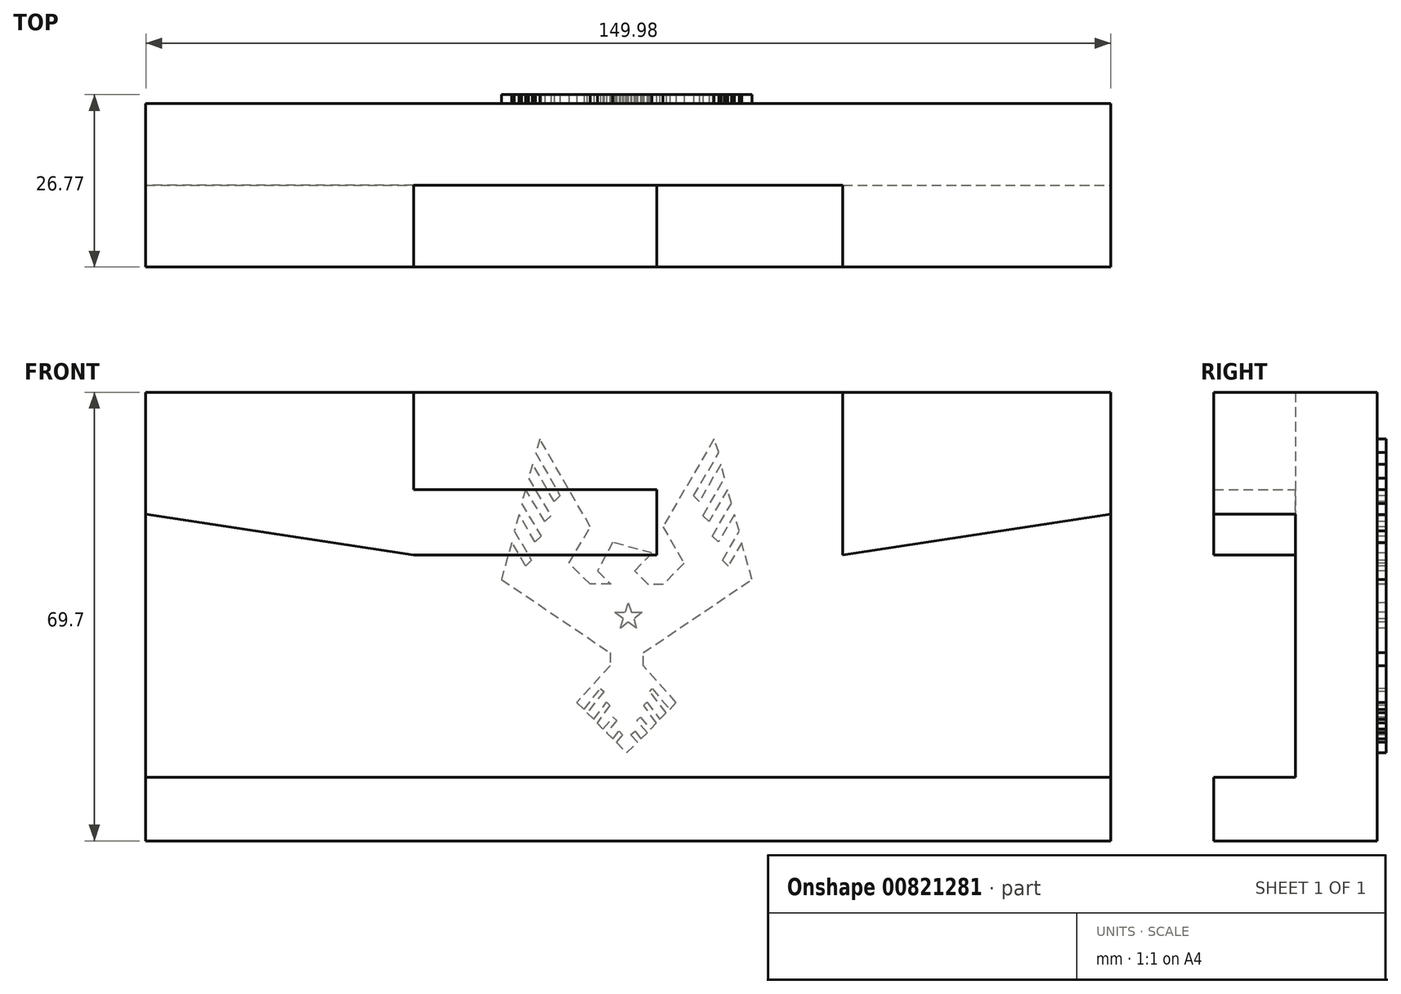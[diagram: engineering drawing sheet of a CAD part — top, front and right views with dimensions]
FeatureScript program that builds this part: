
annotation { "Feature Type Name" : "Feature", "Feature Type Description" : "" }
export const myFeature = defineFeature(function(context is Context, id is Id, definition is map)
    precondition{}
    {
        {
            var Q0;
            Q0=qCreatedBy(makeId("Front.planeOp"),FACE);
            var sketch = newSketch(context, id + "F0", { "sketchPlane" : qUnion([Q0])});
            skLineSegment(sketch, "E0.bottom", {"start": v(75, -34.85) * mm, "end": v(-75, -34.85) * mm});
            skLineSegment(sketch, "E0.top", {"start": v(75, 34.85) * mm, "end": v(-75, 34.85) * mm});
            skLineSegment(sketch, "E0.left", {"start": v(75, -34.85) * mm, "end": v(75, 34.85) * mm});
            skLineSegment(sketch, "E0.right", {"start": v(-75, -34.85) * mm, "end": v(-75, 34.85) * mm});
            skPoint(sketch, "E0.middle", {"position": v(0, 0) * mm});
            skSolve(sketch);
        }
        {
            var Q0;
            Q0=makeQuery(id+"F0.imprint","IMPRINT",FACE,{"disambiguationData":[TD([[makeQuery(id+"F0.imprint","IMPRINT",EDGE,{"derivedFrom":sQuery(id+"F0.wireOp",EDGE,"E0.bottom")}),-1.0]])]});
            extrude(context, id + "F1", {"entities" : qUnion([Q0]), "depth" : 25.4 * mm, "offsetDistance" : 25.4 * mm});
        }
        {
            var Q0;
            Q0=makeQuery(id+"F1.opExtrude","CAP_FACE",FACE,{"disambiguationData":[OSD([sQuery(id+"F0.wireOp",EDGE,"E0.bottom"),sQuery(id+"F0.wireOp",EDGE,"E0.top"),sQuery(id+"F0.wireOp",EDGE,"E0.left"),sQuery(id+"F0.wireOp",EDGE,"E0.right")])],"isStart":false});
            var sketch = newSketch(context, id + "F2", { "sketchPlane" : qUnion([Q0])});
            skLineSegment(sketch, "E1.bottom", {"start": v(33.34, 34.85) * mm, "end": v(-33.34, 34.85) * mm});
            skLineSegment(sketch, "E1.top", {"start": v(33.34, 9.55) * mm, "end": v(-33.34, 9.55) * mm});
            skLineSegment(sketch, "E1.left", {"start": v(33.34, 34.85) * mm, "end": v(33.34, 9.55) * mm});
            skLineSegment(sketch, "E1.right", {"start": v(-33.34, 34.85) * mm, "end": v(-33.34, 9.55) * mm});
            skPoint(sketch, "E1.middle", {"position": v(0, 22.2) * mm});
            skSolve(sketch);
        }
        {
            var Q0;
            Q0=makeQuery(id+"F2.imprint","IMPRINT",FACE,{"disambiguationData":[TD([[makeQuery(id+"F2.imprint","IMPRINT",EDGE,{"derivedFrom":sQuery(id+"F2.wireOp",EDGE,"E1.bottom")}),1.0]])]});
            extrude(context, id + "F3", {"entities" : qUnion([Q0]), "operationType" : NewBodyOperationType.REMOVE, "oppositeDirection" : true, "depth" : 12.7 * mm, "offsetDistance" : 25.4 * mm});
        }
        {
            var Q0;
            Q0=makeQuery(id+"F1.opExtrude","CAP_FACE",FACE,{"disambiguationData":[OSD([sQuery(id+"F0.wireOp",EDGE,"E0.bottom"),sQuery(id+"F0.wireOp",EDGE,"E0.top"),sQuery(id+"F0.wireOp",EDGE,"E0.left"),sQuery(id+"F0.wireOp",EDGE,"E0.right")])],"isStart":false});
            var sketch = newSketch(context, id + "F4", { "sketchPlane" : qUnion([Q0])});
            skLineSegment(sketch, "E2", {"start": v(-33.34, 9.55) * mm, "end": v(-75, 15.95) * mm});
            skLineSegment(sketch, "E3", {"start": v(33.34, 9.55) * mm, "end": v(75, 15.95) * mm});
            skLineSegment(sketch, "E4", {"start": v(-75, 15.95) * mm, "end": v(-75, -25) * mm});
            skLineSegment(sketch, "E5", {"start": v(-75, -25) * mm, "end": v(75, -25) * mm});
            skLineSegment(sketch, "E6", {"start": v(75, -25) * mm, "end": v(75, 15.95) * mm});
            skSolve(sketch);
        }
        {
            var Q0;
            Q0=makeQuery(id+"F4.imprint","IMPRINT",FACE,{"disambiguationData":[TD([[makeQuery(id+"F4.imprint","IMPRINT",EDGE,{"derivedFrom":sQuery(id+"F4.wireOp",EDGE,"E2")}),1.0]])]});
            extrude(context, id + "F5", {"entities" : qUnion([Q0]), "operationType" : NewBodyOperationType.REMOVE, "oppositeDirection" : true, "depth" : 12.7 * mm, "offsetDistance" : 25.4 * mm});
        }
        {
            var Q0;
            {var subQ0=sQuery(id+"F2.wireOp",EDGE,"E1.top");Q0=makeQuery(id+"F5.boolean.opBoolean","MERGE",FACE,{"derivedFrom":[makeQuery(id+"F3.boolean.opBoolean","COPY",FACE,{"derivedFrom":makeQuery(id+"F3.opExtrude","CAP_FACE",FACE,{"disambiguationData":[OSD([sQuery(id+"F2.wireOp",EDGE,"E1.bottom"),subQ0,sQuery(id+"F2.wireOp",EDGE,"E1.left"),sQuery(id+"F2.wireOp",EDGE,"E1.right")])],"isStart":false})}),makeQuery(id+"F5.opExtrude","CAP_FACE",FACE,{"disambiguationData":[OSD([subQ0,sQuery(id+"F4.wireOp",EDGE,"E2"),sQuery(id+"F4.wireOp",EDGE,"E3"),sQuery(id+"F4.wireOp",EDGE,"E4"),sQuery(id+"F4.wireOp",EDGE,"E5"),sQuery(id+"F4.wireOp",EDGE,"E6")])],"isStart":false})]});}
            var sketch = newSketch(context, id + "F6", { "sketchPlane" : qUnion([Q0])});
            skLineSegment(sketch, "E7", {"start": v(-33.34, 9.55) * mm, "end": v(4.4, 9.55) * mm});
            skLineSegment(sketch, "E8", {"start": v(4.4, 9.55) * mm, "end": v(4.4, 19.72) * mm});
            skLineSegment(sketch, "E9", {"start": v(4.4, 19.72) * mm, "end": v(-33.34, 19.72) * mm});
            skSolve(sketch);
        }
        {
            var Q0;
            {var subQ0=sQuery(id+"F6.wireOp",EDGE,"E7");Q0=makeQuery(id+"F6.imprint","IMPRINT",FACE,{"disambiguationData":[TD([[makeQuery(id+"F6.imprint","IMPRINT",EDGE,{"derivedFrom":subQ0}),1.0]])]});}
            extrude(context, id + "F7", {"entities" : qUnion([Q0]), "operationType" : NewBodyOperationType.ADD, "depth" : 12.7 * mm, "offsetDistance" : 25.4 * mm});
        }
        {
            var Q0;
            Q0=makeQuery(id+"F1.opExtrude","CAP_FACE",FACE,{"disambiguationData":[OSD([sQuery(id+"F0.wireOp",EDGE,"E0.bottom"),sQuery(id+"F0.wireOp",EDGE,"E0.top"),sQuery(id+"F0.wireOp",EDGE,"E0.left"),sQuery(id+"F0.wireOp",EDGE,"E0.right")])],"isStart":true});
            var sketch = newSketch(context, id + "F8", { "sketchPlane" : qUnion([Q0])});
            skLineSegment(sketch, "E10", {"start": v(-13.32, 27.6) * mm, "end": v(-5.38, 13.97) * mm});
            skLineSegment(sketch, "E11", {"start": v(-5.38, 13.97) * mm, "end": v(-8.66, 8.3) * mm});
            skLineSegment(sketch, "E12", {"start": v(-8.66, 8.3) * mm, "end": v(-5.43, 5.03) * mm});
            skLineSegment(sketch, "E13", {"start": v(-5.43, 5.03) * mm, "end": v(-3.08, 5.03) * mm});
            skLineSegment(sketch, "E14", {"start": v(-3.08, 5.03) * mm, "end": v(-0.97, 7.1) * mm});
            skLineSegment(sketch, "E15", {"start": v(-0.97, 7.1) * mm, "end": v(-3.68, 9.87) * mm});
            skLineSegment(sketch, "E16", {"start": v(-3.68, 9.87) * mm, "end": v(2.44, 11.55) * mm});
            skLineSegment(sketch, "E17", {"start": v(2.44, 11.55) * mm, "end": v(4.77, 7.1) * mm});
            skLineSegment(sketch, "E18", {"start": v(4.77, 7.1) * mm, "end": v(2.72, 5.06) * mm});
            skLineSegment(sketch, "E19", {"start": v(2.72, 5.06) * mm, "end": v(5.94, 5.06) * mm});
            skLineSegment(sketch, "E20", {"start": v(5.94, 5.06) * mm, "end": v(9.22, 8.3) * mm});
            skLineSegment(sketch, "E21", {"start": v(9.22, 8.3) * mm, "end": v(5.91, 13.98) * mm});
            skLineSegment(sketch, "E22", {"start": v(5.91, 13.98) * mm, "end": v(13.76, 27.6) * mm});
            skLineSegment(sketch, "E23", {"start": v(13.76, 27.6) * mm, "end": v(14.43, 25.49) * mm});
            skLineSegment(sketch, "E24", {"start": v(14.43, 25.49) * mm, "end": v(10.63, 18.77) * mm});
            skLineSegment(sketch, "E25", {"start": v(10.63, 18.77) * mm, "end": v(11.53, 17.89) * mm});
            skLineSegment(sketch, "E26", {"start": v(11.53, 17.89) * mm, "end": v(14.86, 23.66) * mm});
            skLineSegment(sketch, "E27", {"start": v(14.86, 23.66) * mm, "end": v(15.54, 21.52) * mm});
            skLineSegment(sketch, "E28", {"start": v(15.54, 21.52) * mm, "end": v(12.06, 15.69) * mm});
            skLineSegment(sketch, "E29", {"start": v(12.06, 15.69) * mm, "end": v(12.97, 14.79) * mm});
            skLineSegment(sketch, "E30", {"start": v(12.97, 14.79) * mm, "end": v(15.95, 19.76) * mm});
            skLineSegment(sketch, "E31", {"start": v(15.95, 19.76) * mm, "end": v(16.6, 17.6) * mm});
            skLineSegment(sketch, "E32", {"start": v(16.6, 17.6) * mm, "end": v(13.57, 12.51) * mm});
            skLineSegment(sketch, "E33", {"start": v(13.57, 12.51) * mm, "end": v(14.51, 11.58) * mm});
            skLineSegment(sketch, "E34", {"start": v(14.51, 11.58) * mm, "end": v(16.97, 15.85) * mm});
            skLineSegment(sketch, "E35", {"start": v(16.97, 15.85) * mm, "end": v(17.75, 13.3) * mm});
            skLineSegment(sketch, "E36", {"start": v(17.75, 13.3) * mm, "end": v(15.05, 8.78) * mm});
            skLineSegment(sketch, "E37", {"start": v(15.05, 8.78) * mm, "end": v(15.95, 7.89) * mm});
            skLineSegment(sketch, "E38", {"start": v(15.95, 7.89) * mm, "end": v(18.1, 11.5) * mm});
            skLineSegment(sketch, "E39", {"start": v(18.1, 11.5) * mm, "end": v(19.74, 5.79) * mm});
            skLineSegment(sketch, "E40", {"start": v(19.74, 5.79) * mm, "end": v(2.83, -5.61) * mm});
            skLineSegment(sketch, "E41", {"start": v(2.83, -5.61) * mm, "end": v(2.83, -7.63) * mm});
            skLineSegment(sketch, "E42", {"start": v(2.83, -7.63) * mm, "end": v(8.05, -13.36) * mm});
            skLineSegment(sketch, "E43", {"start": v(8.05, -13.36) * mm, "end": v(6.89, -14.42) * mm});
            skLineSegment(sketch, "E44", {"start": v(6.89, -14.42) * mm, "end": v(4.33, -11.2) * mm});
            skLineSegment(sketch, "E45", {"start": v(4.33, -11.2) * mm, "end": v(3.8, -11.61) * mm});
            skLineSegment(sketch, "E46", {"start": v(3.8, -11.61) * mm, "end": v(6.45, -14.96) * mm});
            skLineSegment(sketch, "E47", {"start": v(6.45, -14.96) * mm, "end": v(5.4, -15.93) * mm});
            skLineSegment(sketch, "E48", {"start": v(5.4, -15.93) * mm, "end": v(3.4, -13.31) * mm});
            skLineSegment(sketch, "E49", {"start": v(3.4, -13.31) * mm, "end": v(2.9, -13.76) * mm});
            skLineSegment(sketch, "E50", {"start": v(2.9, -13.76) * mm, "end": v(4.84, -16.53) * mm});
            skLineSegment(sketch, "E51", {"start": v(4.84, -16.53) * mm, "end": v(3.94, -17.48) * mm});
            skLineSegment(sketch, "E52", {"start": v(3.94, -17.48) * mm, "end": v(2.4, -15.64) * mm});
            skLineSegment(sketch, "E53", {"start": v(2.4, -15.64) * mm, "end": v(1.82, -16.13) * mm});
            skLineSegment(sketch, "E54", {"start": v(1.82, -16.13) * mm, "end": v(3.42, -18.03) * mm});
            skLineSegment(sketch, "E55", {"start": v(3.42, -18.03) * mm, "end": v(2.4, -18.98) * mm});
            skLineSegment(sketch, "E56", {"start": v(2.4, -18.98) * mm, "end": v(1.46, -17.8) * mm});
            skLineSegment(sketch, "E57", {"start": v(1.46, -17.8) * mm, "end": v(0.92, -18.38) * mm});
            skLineSegment(sketch, "E58", {"start": v(0.92, -18.38) * mm, "end": v(1.88, -19.5) * mm});
            skLineSegment(sketch, "E59", {"start": v(1.88, -19.5) * mm, "end": v(0.3, -21.15) * mm});
            skLineSegment(sketch, "E60", {"start": v(0.3, -21.15) * mm, "end": v(-1.44, -19.5) * mm});
            skLineSegment(sketch, "E61", {"start": v(-1.44, -19.5) * mm, "end": v(-0.37, -18.38) * mm});
            skLineSegment(sketch, "E62", {"start": v(-0.37, -18.38) * mm, "end": v(-1.02, -17.8) * mm});
            skLineSegment(sketch, "E63", {"start": v(-1.02, -17.8) * mm, "end": v(-1.93, -18.98) * mm});
            skLineSegment(sketch, "E64", {"start": v(-1.93, -18.98) * mm, "end": v(-2.92, -18.03) * mm});
            skLineSegment(sketch, "E65", {"start": v(-2.92, -18.03) * mm, "end": v(-1.31, -16.13) * mm});
            skLineSegment(sketch, "E66", {"start": v(-1.31, -16.13) * mm, "end": v(-1.89, -15.64) * mm});
            skLineSegment(sketch, "E67", {"start": v(-1.89, -15.64) * mm, "end": v(-3.44, -17.48) * mm});
            skLineSegment(sketch, "E68", {"start": v(-3.44, -17.48) * mm, "end": v(-4.33, -16.53) * mm});
            skLineSegment(sketch, "E69", {"start": v(-4.33, -16.53) * mm, "end": v(-2.39, -13.76) * mm});
            skLineSegment(sketch, "E70", {"start": v(-2.39, -13.76) * mm, "end": v(-2.86, -13.31) * mm});
            skLineSegment(sketch, "E71", {"start": v(-2.86, -13.31) * mm, "end": v(-4.88, -15.93) * mm});
            skLineSegment(sketch, "E72", {"start": v(-4.88, -15.93) * mm, "end": v(-5.9, -14.96) * mm});
            skLineSegment(sketch, "E73", {"start": v(-5.9, -14.96) * mm, "end": v(-3.33, -11.61) * mm});
            skLineSegment(sketch, "E74", {"start": v(-3.33, -11.61) * mm, "end": v(-3.71, -11.2) * mm});
            skLineSegment(sketch, "E75", {"start": v(-3.71, -11.2) * mm, "end": v(-6.46, -14.42) * mm});
            skLineSegment(sketch, "E76", {"start": v(-6.46, -14.42) * mm, "end": v(-7.42, -13.36) * mm});
            skLineSegment(sketch, "E77", {"start": v(-7.42, -13.36) * mm, "end": v(-2.31, -7.63) * mm});
            skLineSegment(sketch, "E78", {"start": v(-2.31, -7.63) * mm, "end": v(-2.31, -5.61) * mm});
            skLineSegment(sketch, "E79", {"start": v(-2.31, -5.61) * mm, "end": v(-19.22, 5.79) * mm});
            skLineSegment(sketch, "E80", {"start": v(-19.22, 5.79) * mm, "end": v(-17.6, 11.5) * mm});
            skLineSegment(sketch, "E81", {"start": v(-17.6, 11.5) * mm, "end": v(-15.52, 7.89) * mm});
            skLineSegment(sketch, "E82", {"start": v(-15.52, 7.89) * mm, "end": v(-14.63, 8.78) * mm});
            skLineSegment(sketch, "E83", {"start": v(-14.63, 8.78) * mm, "end": v(-17.26, 13.3) * mm});
            skLineSegment(sketch, "E84", {"start": v(-17.26, 13.3) * mm, "end": v(-16.47, 15.85) * mm});
            skLineSegment(sketch, "E85", {"start": v(-16.47, 15.85) * mm, "end": v(-13.98, 11.58) * mm});
            skLineSegment(sketch, "E86", {"start": v(-13.98, 11.58) * mm, "end": v(-13.05, 12.51) * mm});
            skLineSegment(sketch, "E87", {"start": v(-13.05, 12.51) * mm, "end": v(-16.01, 17.6) * mm});
            skLineSegment(sketch, "E88", {"start": v(-16.01, 17.6) * mm, "end": v(-15.41, 19.76) * mm});
            skLineSegment(sketch, "E89", {"start": v(-15.41, 19.76) * mm, "end": v(-12.51, 14.79) * mm});
            skLineSegment(sketch, "E90", {"start": v(-12.51, 14.79) * mm, "end": v(-11.62, 15.69) * mm});
            skLineSegment(sketch, "E91", {"start": v(-11.62, 15.69) * mm, "end": v(-14.94, 21.52) * mm});
            skLineSegment(sketch, "E92", {"start": v(-14.94, 21.52) * mm, "end": v(-14.36, 23.66) * mm});
            skLineSegment(sketch, "E93", {"start": v(-14.36, 23.66) * mm, "end": v(-11.02, 17.89) * mm});
            skLineSegment(sketch, "E94", {"start": v(-11.02, 17.89) * mm, "end": v(-10.15, 18.77) * mm});
            skLineSegment(sketch, "E95", {"start": v(-10.15, 18.77) * mm, "end": v(-14.07, 25.49) * mm});
            skLineSegment(sketch, "E96", {"start": v(-14.07, 25.49) * mm, "end": v(-13.32, 27.6) * mm});
            skLineSegment(sketch, "E97", {"start": v(0, 2.13) * mm, "end": v(-0.49, 0.68) * mm});
            skLineSegment(sketch, "E98", {"start": v(-0.49, 0.68) * mm, "end": v(-2.13, 0.68) * mm});
            skLineSegment(sketch, "E99", {"start": v(-2.13, 0.68) * mm, "end": v(-0.85, -0.34) * mm});
            skLineSegment(sketch, "E100", {"start": v(-0.85, -0.34) * mm, "end": v(-1.24, -1.8) * mm});
            skLineSegment(sketch, "E101", {"start": v(-1.24, -1.8) * mm, "end": v(0, -0.84) * mm});
            skLineSegment(sketch, "E102", {"start": v(0, -0.84) * mm, "end": v(1.2, -1.79) * mm});
            skLineSegment(sketch, "E103", {"start": v(1.2, -1.79) * mm, "end": v(0.8, -0.34) * mm});
            skLineSegment(sketch, "E104", {"start": v(0.8, -0.34) * mm, "end": v(2.1, 0.68) * mm});
            skLineSegment(sketch, "E105", {"start": v(2.1, 0.68) * mm, "end": v(0.49, 0.68) * mm});
            skLineSegment(sketch, "E106", {"start": v(0.49, 0.68) * mm, "end": v(0, 2.13) * mm});
            skSolve(sketch);
        }
        {
            var Q0;
            Q0=makeQuery(id+"F8.imprint","IMPRINT",FACE,{"disambiguationData":[TD([[makeQuery(id+"F8.imprint","IMPRINT",EDGE,{"derivedFrom":sQuery(id+"F8.wireOp",EDGE,"E10")}),-1.0]])]});
            extrude(context, id + "F9", {"entities" : qUnion([Q0]), "operationType" : NewBodyOperationType.ADD, "depth" : 1.37 * mm, "offsetDistance" : 25.4 * mm});
        }
    });
